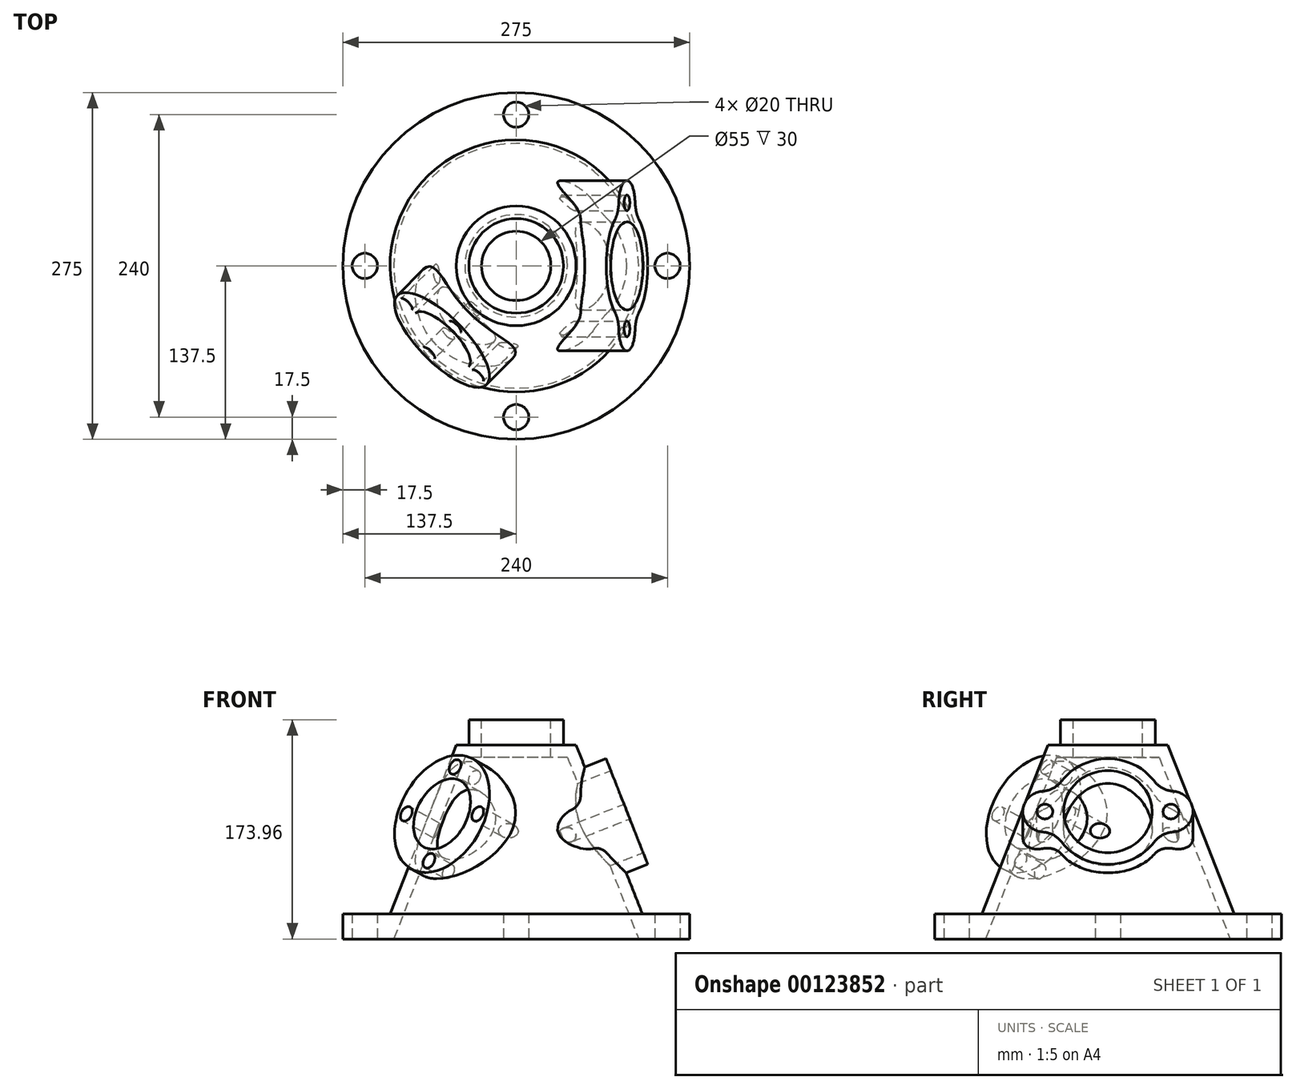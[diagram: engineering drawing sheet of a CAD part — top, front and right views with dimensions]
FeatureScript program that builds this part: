
annotation { "Feature Type Name" : "Feature", "Feature Type Description" : "" }
export const myFeature = defineFeature(function(context is Context, id is Id, definition is map)
    precondition{}
    {
        {
            var Q0;
            Q0=qCreatedBy(makeId("Front.planeOp"),FACE);
            var sketch = newSketch(context, id + "F0", { "sketchPlane" : qUnion([Q0])});
            skLineSegment(sketch, "E0", {"start": v(-27.5, 0) * mm, "end": v(-27.5, 4) * mm});
            skLineSegment(sketch, "E1", {"start": v(-27.5, 4) * mm, "end": v(-20, 4) * mm});
            skLineSegment(sketch, "E2", {"start": v(-20, 4) * mm, "end": v(-9.5, 30.8) * mm});
            skLineSegment(sketch, "E3", {"start": v(-9.5, 30.8) * mm, "end": v(-7.5, 30.8) * mm});
            skLineSegment(sketch, "E4", {"start": v(-7.5, 30.8) * mm, "end": v(-7.5, 34.8) * mm});
            skLineSegment(sketch, "E5", {"start": v(-7.5, 34.8) * mm, "end": v(-5.5, 34.8) * mm});
            skLineSegment(sketch, "E6", {"start": v(-5.5, 34.8) * mm, "end": v(-5.5, 28.8) * mm});
            skLineSegment(sketch, "E7", {"start": v(-8.14, 28.8) * mm, "end": v(-19.42, 0) * mm});
            skLineSegment(sketch, "E8", {"start": v(-27.5, 0) * mm, "end": v(-19.42, 0) * mm});
            skLineSegment(sketch, "E9", {"start": v(-5.5, 28.8) * mm, "end": v(-8.14, 28.8) * mm});
            skLineSegment(sketch, "E10", {"start": v(0, 60.05) * mm, "end": v(0, -17.62) * mm, "construction": true});
            skSolve(sketch);
        }
        {
            var Q0;
            Q0 = qSketchRegion(id + "F0", true);
            var Q1;
            Q1=sQuery(id+"F0.wireOp",EDGE,"E10");
            revolve(context, id + "F1", {"entities" : qUnion([Q0]), "axis" : qUnion([Q1]), "revolveType" : RevolveType.FULL});
        }
        {
            var Q0;
            Q0=makeQuery(id+"F1.opRevolve","SWEPT_FACE",FACE,{"disambiguationData":[OSD([sQuery(id+"F0.wireOp",EDGE,"E5")])]});
            var sketch = newSketch(context, id + "F2", { "sketchPlane" : qUnion([Q0])});
            skLineSegment(sketch, "E11", {"start": v(0, 33.46) * mm, "end": v(0, -33.05) * mm, "construction": true});
            skLineSegment(sketch, "E12", {"start": v(-23.35, 23.35) * mm, "end": v(25.48, -25.48) * mm, "construction": true});
            skSolve(sketch);
        }
        {
            var Q0;
            Q0=sQuery(id+"F2.wireOp",EDGE,"E11");
            var Q1;
            Q1=qCreatedBy(makeId("Right.planeOp"),FACE);
            cPlane(context, id + "F3", {"entities" : qUnion([Q0, Q1]), "cplaneType" : CPlaneType.LINE_ANGLE, "offset" : 25 * mm, "angle" : 21.5 * degree, "width" : 150 * mm, "height" : 150 * mm});
        }
        {
            var Q0;
            Q0=qCreatedBy(id+"F3.planeOp",FACE);
            cPlane(context, id + "F4", {"entities" : qUnion([Q0]), "cplaneType" : CPlaneType.OFFSET, "offset" : 11 * mm, "oppositeDirection" : true, "width" : 150 * mm, "height" : 150 * mm});
        }
        {
            var Q0;
            Q0=qCreatedBy(id+"F4.planeOp",FACE);
            var sketch = newSketch(context, id + "F5", { "sketchPlane" : qUnion([Q0])});
            skLineSegment(sketch, "E13", {"start": v(36.98, 12.37) * mm, "end": v(-37.95, 12.37) * mm, "construction": true});
            skArc(sketch, "E14", {"start": v(7.36, 17.55) * mm, "mid": v(0, 21.37) * mm, "end": v(-7.36, 17.55) * mm});
            skArc(sketch, "E15", {"start": v(10.3, 8.88) * mm, "mid": v(13.5, 12.37) * mm, "end": v(10.3, 15.86) * mm});
            skArc(sketch, "E16.MirrorCS", {"start": v(-10.3, 8.88) * mm, "mid": v(-13.5, 12.37) * mm, "end": v(-10.3, 15.86) * mm});
            skArc(sketch, "E17.trimOffspring", {"start": v(-7.36, 7.2) * mm, "mid": v(0, 3.37) * mm, "end": v(7.36, 7.2) * mm});
            skPoint(sketch, "E18.visualSharp", {"position": v(8.44, 15.5) * mm});
            skArc(sketch, "E18.filletArc", {"start": v(7.36, 17.55) * mm, "mid": v(8.64, 16.38) * mm, "end": v(10.3, 15.86) * mm});
            skPoint(sketch, "E19.visualSharp", {"position": v(8.44, 9.24) * mm});
            skArc(sketch, "E19.filletArc", {"start": v(10.3, 8.88) * mm, "mid": v(8.64, 8.37) * mm, "end": v(7.36, 7.2) * mm});
            skPoint(sketch, "E20.visualSharp", {"position": v(-8.44, 9.24) * mm});
            skArc(sketch, "E20.filletArc", {"start": v(-7.36, 7.2) * mm, "mid": v(-8.64, 8.37) * mm, "end": v(-10.3, 8.88) * mm});
            skPoint(sketch, "E21.visualSharp", {"position": v(-8.44, 15.5) * mm});
            skArc(sketch, "E21.filletArc", {"start": v(-10.3, 15.86) * mm, "mid": v(-8.64, 16.38) * mm, "end": v(-7.36, 17.55) * mm});
            skSolve(sketch);
        }
        {
            var Q0;
            Q0=makeQuery(id+"F5.imprint","IMPRINT",FACE,{"disambiguationData":[TD([[makeQuery(id+"F5.imprint","IMPRINT",EDGE,{"derivedFrom":sQuery(id+"F5.wireOp",EDGE,"E14")}),1.0]])]});
            extrude(context, id + "F6", {"entities" : qUnion([Q0]), "operationType" : NewBodyOperationType.ADD, "endBound" : BoundingType.UP_TO_NEXT, "depth" : 25 * mm});
        }
        {
            var Q0;
            Q0=makeQuery(id+"F6.opExtrude","CAP_FACE",FACE,{"disambiguationData":[OSD([sQuery(id+"F5.wireOp",EDGE,"E14"),sQuery(id+"F5.wireOp",EDGE,"E15"),sQuery(id+"F5.wireOp",EDGE,"E16.MirrorCS"),sQuery(id+"F5.wireOp",EDGE,"E17.trimOffspring"),sQuery(id+"F5.wireOp",EDGE,"E18.filletArc"),sQuery(id+"F5.wireOp",EDGE,"E19.filletArc"),sQuery(id+"F5.wireOp",EDGE,"E20.filletArc"),sQuery(id+"F5.wireOp",EDGE,"E21.filletArc")])],"isStart":true});
            var sketch = newSketch(context, id + "F7", { "sketchPlane" : qUnion([Q0])});
            skPoint(sketch, "E22", {"position": v(-10, 12.37) * mm});
            skPoint(sketch, "E23", {"position": v(10, 12.37) * mm});
            skPoint(sketch, "E24", {"position": v(0, 12.37) * mm});
            skSolve(sketch);
        }
        {
            var Q0;
            Q0=sQuery(id+"F7.wireOp",VERTEX,"E24");
            var Q1;
            Q1=makeQuery(id+"F1.opRevolve","SWEPT_BODY",BODY,{"disambiguationData":[OSD([sQuery(id+"F0.wireOp",EDGE,"E0"),sQuery(id+"F0.wireOp",EDGE,"E1"),sQuery(id+"F0.wireOp",EDGE,"E2"),sQuery(id+"F0.wireOp",EDGE,"E3"),sQuery(id+"F0.wireOp",EDGE,"E4"),sQuery(id+"F0.wireOp",EDGE,"E5"),sQuery(id+"F0.wireOp",EDGE,"E6"),sQuery(id+"F0.wireOp",EDGE,"E7"),sQuery(id+"F0.wireOp",EDGE,"E8"),sQuery(id+"F0.wireOp",EDGE,"E9")])]});
            hole(context, id + "F8", {"style" : HoleStyle.SIMPLE, "endStyle" : HoleEndStyle.BLIND, "holeDiameter" : 14 * mm, "holeDepth" : 11 * mm, "locations" : qUnion([Q0]), "scope" : qUnion([Q1])});
        }
        {
            var Q0;
            Q0=sQuery(id+"F7.wireOp",VERTEX,"E22");
            var Q1;
            Q1=sQuery(id+"F7.wireOp",VERTEX,"E23");
            var Q2;
            Q2=makeQuery(id+"F1.opRevolve","SWEPT_BODY",BODY,{"disambiguationData":[OSD([sQuery(id+"F0.wireOp",EDGE,"E0"),sQuery(id+"F0.wireOp",EDGE,"E1"),sQuery(id+"F0.wireOp",EDGE,"E2"),sQuery(id+"F0.wireOp",EDGE,"E3"),sQuery(id+"F0.wireOp",EDGE,"E4"),sQuery(id+"F0.wireOp",EDGE,"E5"),sQuery(id+"F0.wireOp",EDGE,"E6"),sQuery(id+"F0.wireOp",EDGE,"E7"),sQuery(id+"F0.wireOp",EDGE,"E8"),sQuery(id+"F0.wireOp",EDGE,"E9")])]});
            hole(context, id + "F9", {"style" : HoleStyle.SIMPLE, "endStyle" : HoleEndStyle.BLIND, "holeDiameter" : 2.5 * mm, "holeDepth" : 11 * mm, "locations" : qUnion([Q0, Q1]), "scope" : qUnion([Q2])});
        }
        {
            var Q0;
            Q0=sQuery(id+"F0.wireOp",EDGE,"E10");
            var Q1;
            Q1=qCreatedBy(makeId("Front.planeOp"),FACE);
            cPlane(context, id + "F10", {"entities" : qUnion([Q0, Q1]), "cplaneType" : CPlaneType.LINE_ANGLE, "offset" : 25 * mm, "angle" : 45 * degree, "width" : 150 * mm, "height" : 150 * mm});
        }
        {
            var Q0;
            Q0=sQuery(id+"F2.wireOp",EDGE,"E12");
            var Q1;
            Q1=qCreatedBy(id+"F10.planeOp",FACE);
            cPlane(context, id + "F11", {"entities" : qUnion([Q0, Q1]), "cplaneType" : CPlaneType.LINE_ANGLE, "offset" : 25 * mm, "angle" : 158.5 * degree, "width" : 150 * mm, "height" : 150 * mm});
        }
        {
            var Q0;
            Q0=qCreatedBy(id+"F11.planeOp",FACE);
            cPlane(context, id + "F12", {"entities" : qUnion([Q0]), "cplaneType" : CPlaneType.OFFSET, "offset" : 10 * mm, "oppositeDirection" : true, "width" : 150 * mm, "height" : 150 * mm});
        }
        {
            var Q0;
            Q0=qCreatedBy(id+"F12.planeOp",FACE);
            var sketch = newSketch(context, id + "F13", { "sketchPlane" : qUnion([Q0])});
            skLineSegment(sketch, "E25", {"start": v(42.79, 28.86) * mm, "end": v(-46.76, -3.96) * mm, "construction": true});
            skCircle(sketch, "E26", {"center": v(-4.26, 11.62) * mm, "radius": 10 * mm});
            skCircle(sketch, "E27", {"center": v(-4.26, 11.62) * mm, "radius": 8 * mm, "construction": true});
            skPoint(sketch, "E28", {"position": v(-7.01, 19.13) * mm});
            skPoint(sketch, "E29", {"position": v(-11.77, 8.86) * mm});
            skPoint(sketch, "E30", {"position": v(-1.5, 4.1) * mm});
            skPoint(sketch, "E31", {"position": v(3.25, 14.37) * mm});
            skSolve(sketch);
        }
        {
            var Q0;
            Q0 = qSketchRegion(id + "F13", true);
            extrude(context, id + "F14", {"entities" : qUnion([Q0]), "operationType" : NewBodyOperationType.ADD, "endBound" : BoundingType.UP_TO_NEXT, "depth" : 25 * mm});
        }
        {
            var Q0;
            Q0=sQuery(id+"F13.wireOp",VERTEX,"E26.center");
            var Q1;
            Q1=makeQuery(id+"F1.opRevolve","SWEPT_BODY",BODY,{"disambiguationData":[OSD([sQuery(id+"F0.wireOp",EDGE,"E0"),sQuery(id+"F0.wireOp",EDGE,"E1"),sQuery(id+"F0.wireOp",EDGE,"E2"),sQuery(id+"F0.wireOp",EDGE,"E3"),sQuery(id+"F0.wireOp",EDGE,"E4"),sQuery(id+"F0.wireOp",EDGE,"E5"),sQuery(id+"F0.wireOp",EDGE,"E6"),sQuery(id+"F0.wireOp",EDGE,"E7"),sQuery(id+"F0.wireOp",EDGE,"E8"),sQuery(id+"F0.wireOp",EDGE,"E9")])]});
            hole(context, id + "F15", {"style" : HoleStyle.SIMPLE, "endStyle" : HoleEndStyle.BLIND, "oppositeDirection" : true, "holeDiameter" : 12 * mm, "holeDepth" : 10 * mm, "locations" : qUnion([Q0]), "scope" : qUnion([Q1])});
        }
        {
            var Q0;
            Q0=sQuery(id+"F13.wireOp",VERTEX,"E28");
            var Q1;
            Q1=sQuery(id+"F13.wireOp",VERTEX,"E31");
            var Q2;
            Q2=sQuery(id+"F13.wireOp",VERTEX,"E30");
            var Q3;
            Q3=sQuery(id+"F13.wireOp",VERTEX,"E29");
            var Q4;
            Q4=makeQuery(id+"F1.opRevolve","SWEPT_BODY",BODY,{"disambiguationData":[OSD([sQuery(id+"F0.wireOp",EDGE,"E0"),sQuery(id+"F0.wireOp",EDGE,"E1"),sQuery(id+"F0.wireOp",EDGE,"E2"),sQuery(id+"F0.wireOp",EDGE,"E3"),sQuery(id+"F0.wireOp",EDGE,"E4"),sQuery(id+"F0.wireOp",EDGE,"E5"),sQuery(id+"F0.wireOp",EDGE,"E6"),sQuery(id+"F0.wireOp",EDGE,"E7"),sQuery(id+"F0.wireOp",EDGE,"E8"),sQuery(id+"F0.wireOp",EDGE,"E9")])]});
            hole(context, id + "F16", {"style" : HoleStyle.SIMPLE, "endStyle" : HoleEndStyle.BLIND, "oppositeDirection" : true, "holeDiameter" : 2.5 * mm, "holeDepth" : 10 * mm, "locations" : qUnion([Q0, Q1, Q2, Q3]), "scope" : qUnion([Q4])});
        }
        {
            var Q0;
            Q0=qCreatedBy(makeId("Top.planeOp"),FACE);
            var sketch = newSketch(context, id + "F17", { "sketchPlane" : qUnion([Q0])});
            skCircle(sketch, "E32", {"center": v(0, 0) * mm, "radius": 24 * mm, "construction": true});
            skPoint(sketch, "E33", {"position": v(0, 24) * mm});
            skPoint(sketch, "E34", {"position": v(24, 0) * mm});
            skPoint(sketch, "E35", {"position": v(0, -24) * mm});
            skPoint(sketch, "E36", {"position": v(-24, 0) * mm});
            skSolve(sketch);
        }
        {
            var Q0;
            Q0=sQuery(id+"F17.wireOp",VERTEX,"E36");
            var Q1;
            Q1=sQuery(id+"F17.wireOp",VERTEX,"E35");
            var Q2;
            Q2=sQuery(id+"F17.wireOp",VERTEX,"E34");
            var Q3;
            Q3=sQuery(id+"F17.wireOp",VERTEX,"E33");
            var Q4;
            Q4=makeQuery(id+"F1.opRevolve","SWEPT_BODY",BODY,{"disambiguationData":[OSD([sQuery(id+"F0.wireOp",EDGE,"E0"),sQuery(id+"F0.wireOp",EDGE,"E1"),sQuery(id+"F0.wireOp",EDGE,"E2"),sQuery(id+"F0.wireOp",EDGE,"E3"),sQuery(id+"F0.wireOp",EDGE,"E4"),sQuery(id+"F0.wireOp",EDGE,"E5"),sQuery(id+"F0.wireOp",EDGE,"E6"),sQuery(id+"F0.wireOp",EDGE,"E7"),sQuery(id+"F0.wireOp",EDGE,"E8"),sQuery(id+"F0.wireOp",EDGE,"E9")])]});
            hole(context, id + "F18", {"style" : HoleStyle.SIMPLE, "endStyle" : HoleEndStyle.BLIND, "oppositeDirection" : true, "holeDiameter" : 4 * mm, "holeDepth" : 4 * mm, "locations" : qUnion([Q0, Q1, Q2, Q3]), "scope" : qUnion([Q4])});
        }
        {
            var Q0;
            Q0=makeQuery(id+"F1.opRevolve","SWEPT_BODY",BODY,{"disambiguationData":[OSD([sQuery(id+"F0.wireOp",EDGE,"E0"),sQuery(id+"F0.wireOp",EDGE,"E1"),sQuery(id+"F0.wireOp",EDGE,"E2"),sQuery(id+"F0.wireOp",EDGE,"E3"),sQuery(id+"F0.wireOp",EDGE,"E4"),sQuery(id+"F0.wireOp",EDGE,"E5"),sQuery(id+"F0.wireOp",EDGE,"E6"),sQuery(id+"F0.wireOp",EDGE,"E7"),sQuery(id+"F0.wireOp",EDGE,"E8"),sQuery(id+"F0.wireOp",EDGE,"E9")])]});
            var Q1;
            Q1=qCreatedBy(makeId("Origin.pointOp"),VERTEX);
            transform(context, id + "F19", {"entities" : qUnion([Q0]), "transformType" : TransformType.SCALE_UNIFORMLY, "scale" : 5, "scalePoint" : qUnion([Q1]), "makeCopy" : false});
        }
    });
